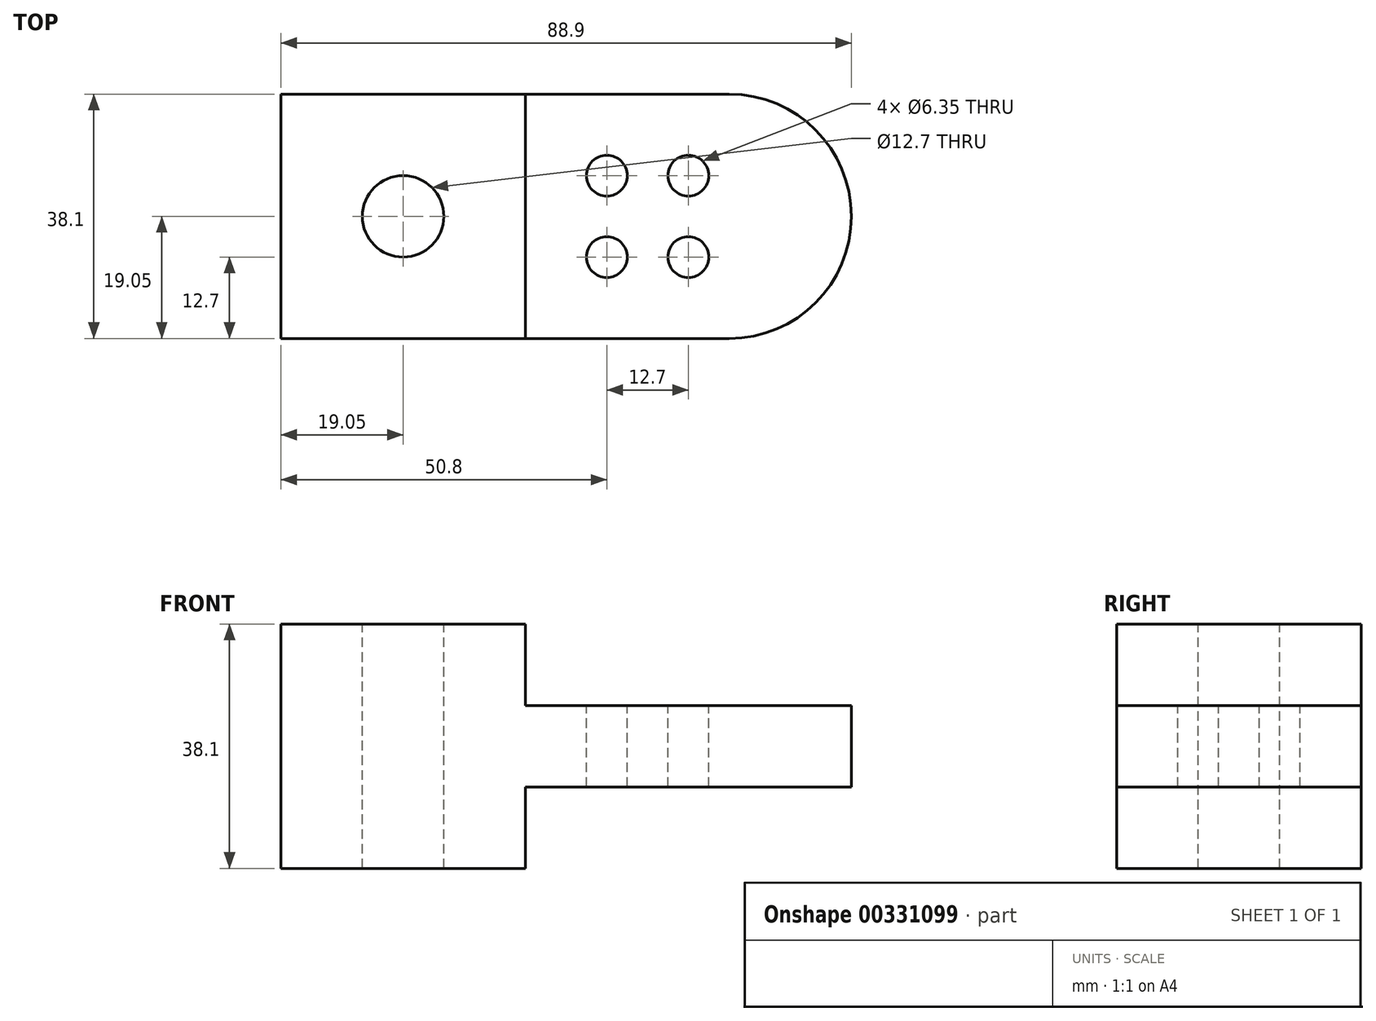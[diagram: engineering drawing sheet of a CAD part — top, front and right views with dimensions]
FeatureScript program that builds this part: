
annotation { "Feature Type Name" : "Feature", "Feature Type Description" : "" }
export const myFeature = defineFeature(function(context is Context, id is Id, definition is map)
    precondition{}
    {
        {
            var Q0;
            Q0=qCreatedBy(makeId("Front.planeOp"),FACE);
            var sketch = newSketch(context, id + "F0", { "sketchPlane" : qUnion([Q0])});
            skLineSegment(sketch, "E0", {"start": v(0, 0) * mm, "end": v(0, 38.1) * mm});
            skLineSegment(sketch, "E1", {"start": v(0, 38.1) * mm, "end": v(38.1, 38.1) * mm});
            skLineSegment(sketch, "E2", {"start": v(38.1, 38.1) * mm, "end": v(38.1, 25.4) * mm});
            skLineSegment(sketch, "E3", {"start": v(38.1, 25.4) * mm, "end": v(88.9, 25.4) * mm});
            skLineSegment(sketch, "E4", {"start": v(88.9, 25.4) * mm, "end": v(88.9, 12.7) * mm});
            skLineSegment(sketch, "E5", {"start": v(88.9, 12.7) * mm, "end": v(38.1, 12.7) * mm});
            skLineSegment(sketch, "E6", {"start": v(38.1, 12.7) * mm, "end": v(38.1, 0) * mm});
            skLineSegment(sketch, "E7", {"start": v(38.1, 0) * mm, "end": v(0, 0) * mm});
            skSolve(sketch);
        }
        {
            var Q0;
            Q0 = qSketchRegion(id + "F0", true);
            extrude(context, id + "F1", {"entities" : qUnion([Q0]), "depth" : 38.1 * mm});
        }
        {
            var Q0;
            Q0=makeQuery(id+"F1.opExtrude","CAP_EDGE",EDGE,{"disambiguationData":[OSD([sQuery(id+"F0.wireOp",EDGE,"E4")])],"isStart":false});
            var Q1;
            Q1=makeQuery(id+"F1.opExtrude","CAP_EDGE",EDGE,{"disambiguationData":[OSD([sQuery(id+"F0.wireOp",EDGE,"E4")])],"isStart":true});
            fillet(context, id + "F2", {"entities" : qUnion([Q0, Q1]), "radius" : 19.05 * mm, "tangentPropagation" : true, "allowEdgeOverflow" : false});
        }
        {
            var Q0;
            Q0=makeQuery(id+"F1.opExtrude","SWEPT_FACE",FACE,{"disambiguationData":[OSD([sQuery(id+"F0.wireOp",EDGE,"E1")])]});
            var sketch = newSketch(context, id + "F3", { "sketchPlane" : qUnion([Q0])});
            skLineSegment(sketch, "E8", {"start": v(19.05, 0) * mm, "end": v(19.05, -38.1) * mm});
            skLineSegment(sketch, "E9", {"start": v(38.1, -19.05) * mm, "end": v(0, -19.05) * mm});
            skCircle(sketch, "E10", {"center": v(19.05, -19.05) * mm, "radius": 6.35 * mm});
            skSolve(sketch);
        }
        {
            var Q0;
            Q0 = qSketchRegion(id + "F3", true);
            extrude(context, id + "F4", {"entities" : qUnion([Q0]), "operationType" : NewBodyOperationType.REMOVE, "oppositeDirection" : true, "depth" : 76.2 * mm});
        }
        {
            var Q0;
            Q0=makeQuery(id+"F1.opExtrude","SWEPT_FACE",FACE,{"disambiguationData":[OSD([sQuery(id+"F0.wireOp",EDGE,"E3")])]});
            var sketch = newSketch(context, id + "F5", { "sketchPlane" : qUnion([Q0])});
            skLineSegment(sketch, "E11", {"start": v(38.1, 0) * mm, "end": v(50.8, 0) * mm});
            skLineSegment(sketch, "E12", {"start": v(50.8, 0) * mm, "end": v(63.5, 0) * mm});
            skLineSegment(sketch, "E13", {"start": v(63.5, 0) * mm, "end": v(63.5, -12.7) * mm});
            skLineSegment(sketch, "E14", {"start": v(63.5, -12.7) * mm, "end": v(50.8, -12.7) * mm});
            skLineSegment(sketch, "E15", {"start": v(50.8, -12.7) * mm, "end": v(50.8, -25.4) * mm});
            skLineSegment(sketch, "E16", {"start": v(50.8, -25.4) * mm, "end": v(63.5, -25.4) * mm});
            skCircle(sketch, "E17", {"center": v(50.8, -12.7) * mm, "radius": 3.18 * mm});
            skCircle(sketch, "E18", {"center": v(63.5, -12.7) * mm, "radius": 3.18 * mm});
            skCircle(sketch, "E19", {"center": v(50.8, -25.4) * mm, "radius": 3.18 * mm});
            skCircle(sketch, "E20", {"center": v(63.5, -25.4) * mm, "radius": 3.18 * mm});
            skSolve(sketch);
        }
        {
            var Q0;
            Q0 = qSketchRegion(id + "F5", true);
            extrude(context, id + "F6", {"entities" : qUnion([Q0]), "operationType" : NewBodyOperationType.REMOVE, "oppositeDirection" : true, "depth" : 101.6 * mm});
        }
    });
